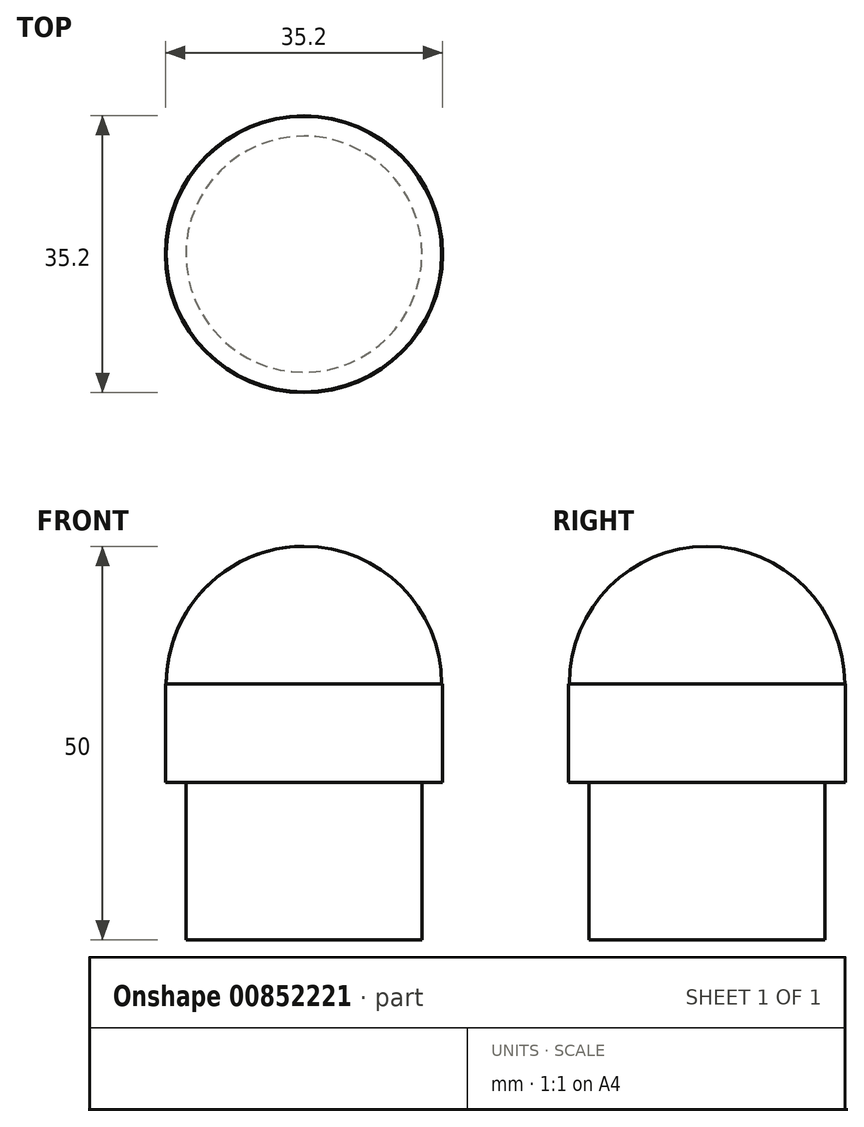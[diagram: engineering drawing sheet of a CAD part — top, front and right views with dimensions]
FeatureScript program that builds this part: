
annotation { "Feature Type Name" : "Feature", "Feature Type Description" : "" }
export const myFeature = defineFeature(function(context is Context, id is Id, definition is map)
    precondition{}
    {
        {
            var Q0;
            Q0=qCreatedBy(makeId("Front.planeOp"),FACE);
            var sketch = newSketch(context, id + "F0", { "sketchPlane" : qUnion([Q0])});
            skLineSegment(sketch, "E0", {"start": v(0, 0) * mm, "end": v(-15, 0) * mm});
            skLineSegment(sketch, "E1", {"start": v(-15, 0) * mm, "end": v(-15, 20) * mm});
            skLineSegment(sketch, "E2", {"start": v(-15, 20) * mm, "end": v(-17.6, 20) * mm});
            skLineSegment(sketch, "E3", {"start": v(-17.6, 20) * mm, "end": v(-17.6, 32.5) * mm});
            skLineSegment(sketch, "E4", {"start": v(-17.6, 32.5) * mm, "end": v(-17.5, 32.5) * mm});
            skArc(sketch, "E5", {"start": v(0, 50) * mm, "mid": v(-12.37, 44.87) * mm, "end": v(-17.5, 32.5) * mm});
            skLineSegment(sketch, "E6", {"start": v(0, 50) * mm, "end": v(0, 0) * mm});
            skSolve(sketch);
        }
        {
            var Q0;
            Q0 = qSketchRegion(id + "F0", true);
            var Q1;
            Q1=sQuery(id+"F0.wireOp",EDGE,"E6");
            revolve(context, id + "F1", {"surfaceOperationType" : NewSurfaceOperationType.NEW, "entities" : qUnion([Q0]), "axis" : qUnion([Q1]), "revolveType" : RevolveType.FULL});
        }
    });
